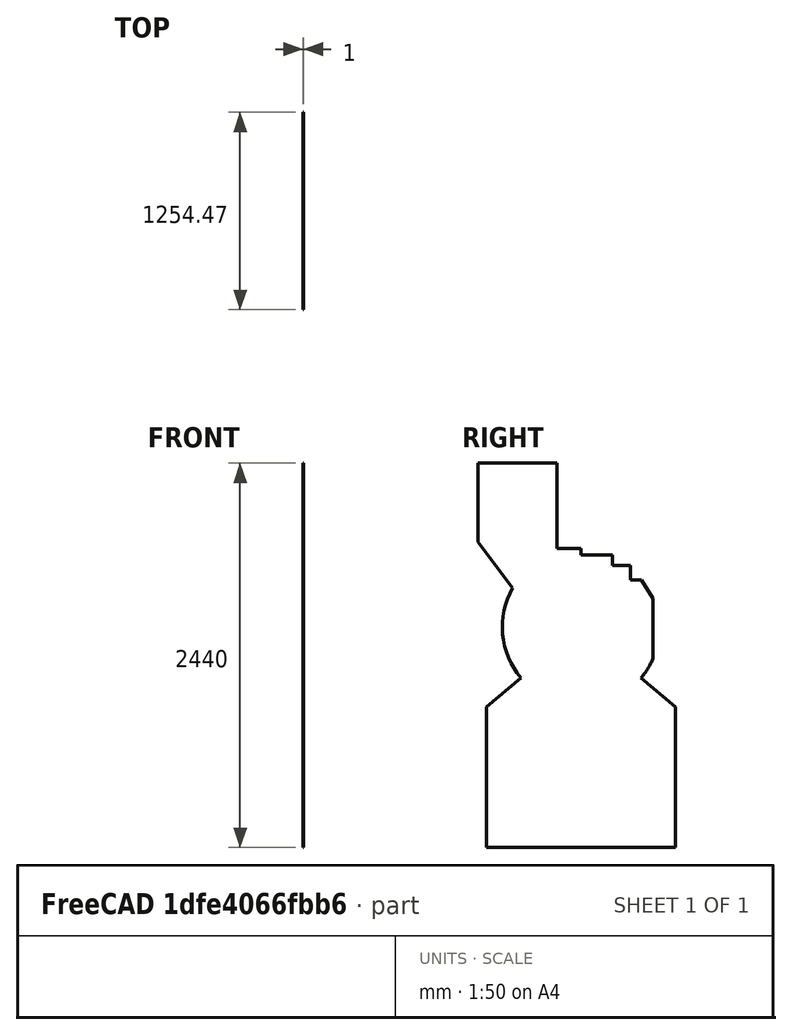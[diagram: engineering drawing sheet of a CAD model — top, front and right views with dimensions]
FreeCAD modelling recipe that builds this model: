
FCSTD DOCUMENT
Label: Shell Back
objects: Sketcher::SketchObject×1, PartDesign::Pad×1
note: 3 computed .brp shape members not serialized (recipe doc carries the construction recipe); baked Part::Feature solids carry a one-line shape summary decoded from their .brp

FEATURE [Sketcher::SketchObject] Sketch
  Placement = pos=(-500,0,0) rot=(0.57735,0.57735,0.57735;2.0944rad)
  sketch-geometry (20):
    g0: ArcOfCircle CenterX=0 CenterY=0 CenterZ=0 NormalX=0 NormalY=0 NormalZ=1 Radius=500 StartAngle=2.6242 EndAngle=3.84621
    g1: LineSegment StartX=-434.557 StartY=247.306 StartZ=0 EndX=-654.474 EndY=540 EndZ=0
    g2: LineSegment StartX=-152.007 StartY=500 StartZ=0 EndX=3.79032e-05 EndY=500 EndZ=0
    g3: LineSegment StartX=3.79032e-05 StartY=500 StartZ=0 EndX=3.79032e-05 EndY=458.471 EndZ=0
    g4: LineSegment StartX=3.79032e-05 StartY=458.471 StartZ=0 EndX=199.509 EndY=458.471 EndZ=0
    g5: LineSegment StartX=199.509 StartY=458.471 StartZ=0 EndX=199.509 EndY=390 EndZ=0
    g6: LineSegment StartX=199.509 StartY=390 StartZ=0 EndX=312.89 EndY=390 EndZ=0
    g7: LineSegment StartX=312.89 StartY=390 StartZ=0 EndX=312.89 EndY=297.137 EndZ=0
    g8: LineSegment StartX=312.89 StartY=297.137 StartZ=0 EndX=382.89 EndY=297.137 EndZ=0
    g9: LineSegment StartX=458.29 StartY=180.074 StartZ=0 EndX=458.29 EndY=-199.926 EndZ=0
    g10: LineSegment StartX=-654.474 StartY=1040 StartZ=0 EndX=-654.474 EndY=540 EndZ=0
    g11: LineSegment StartX=-380.931 StartY=-323.87 StartZ=0 EndX=-600 EndY=-507.691 EndZ=0
    g12: LineSegment StartX=-600 StartY=-507.691 StartZ=0 EndX=-600 EndY=-1400 EndZ=0
    g13: LineSegment StartX=-600 StartY=-1400 StartZ=0 EndX=600 EndY=-1400 EndZ=0
    g14: LineSegment StartX=600 StartY=-1400 StartZ=0 EndX=600 EndY=-507.691 EndZ=0
    g15: LineSegment StartX=600 StartY=-507.691 StartZ=0 EndX=380.931 EndY=-323.87 EndZ=0
    g16: LineSegment StartX=382.89 StartY=297.137 StartZ=0 EndX=458.29 EndY=180.074 EndZ=0
    g17: ArcOfCircle CenterX=0 CenterY=0 CenterZ=0 NormalX=0 NormalY=0 NormalZ=1 Radius=500 StartAngle=5.57857 EndAngle=5.87183
    g18: LineSegment StartX=-654.474 StartY=1040 StartZ=0 EndX=-152.007 EndY=1040 EndZ=0
    g19: LineSegment StartX=-152.007 StartY=1040 StartZ=0 EndX=-152.007 EndY=500 EndZ=0
  constraints (65):
    c: Radius(g0) = 500
    c: DistanceX(g0) = 0
    c: DistanceY(g0) = 0
    c: PointOnObject(g3,g0)
    c: Horizontal(g2)
    c: Vertical(g3)
    c: Coincident(g4,g3)
    c: PointOnObject(g5,g0)
    c: Horizontal(g4)
    c: Vertical(g5)
    c: Coincident(g6,g5)
    c: PointOnObject(g7,g0)
    c: Horizontal(g6)
    c: Vertical(g7)
    c: Coincident(g8,g7)
    c: Horizontal(g8)
    c: DistanceX(g1) = -654.474
    c: DistanceY(g1) = 540
    c: Coincident(g2,g3)
    c: Coincident(g4,g5)
    c: Coincident(g6,g7)
    c: Coincident(g9,g17)
    c: Vertical(g9)
    c: Distance(g9) = 380
    c: DistanceX(g2) = -152.007
    c: DistanceY(g2) = 500
    c: DistanceX(g5) = 199.509
    c: DistanceY(g5) = 390
    c: Distance(g8) = 70
    c: Coincident(g10,g1)
    c: Vertical(g10)
    c: Distance(g10) = 500
    c: Coincident(g12,g11)
    c: Vertical(g12)
    c: Horizontal(g13)
    c: Coincident(g14,g13)
    c: Vertical(g14)
    c: Coincident(g15,g14)
    c: Coincident(g13,g12)
    c: Equal(g14,g12)
    c: DistanceX(g13) = 600
    c: DistanceY(g13) = -1400
    c: Angle(g12,g11) = 2.26893
    c: Angle(g15,g14) = 2.26893
    c: Distance(g12) = 892.309
    c: Distance(g13) = 1200
    c: Coincident(g16,g8)
    c: Coincident(g16,g9)
    c: Distance(g16) = 139.244
    c: Distance(g7) = 92.8633
    c: Equal(g0,g17)
    c: Coincident(g0,g17)
    c: PointOnObject(g16,g17)
    c: PointOnObject(g16,g17)
    c: PointOnObject(g16,g17)
    c: PointOnObject(g16,g17)
    c: Coincident(g0,g11)
    c: Coincident(g15,g17)
    c: Coincident(g0,g1)
    c: Distance(g1) = 366.106
    c: Coincident(g18,g10)
    c: Horizontal(g18)
    c: Coincident(g19,g18)
    c: Coincident(g19,g2)
    c: Vertical(g19)
FEATURE [PartDesign::Pad] Pad
  Length = 1
  MirroredExtent = false
  Sketch = -> Sketch
